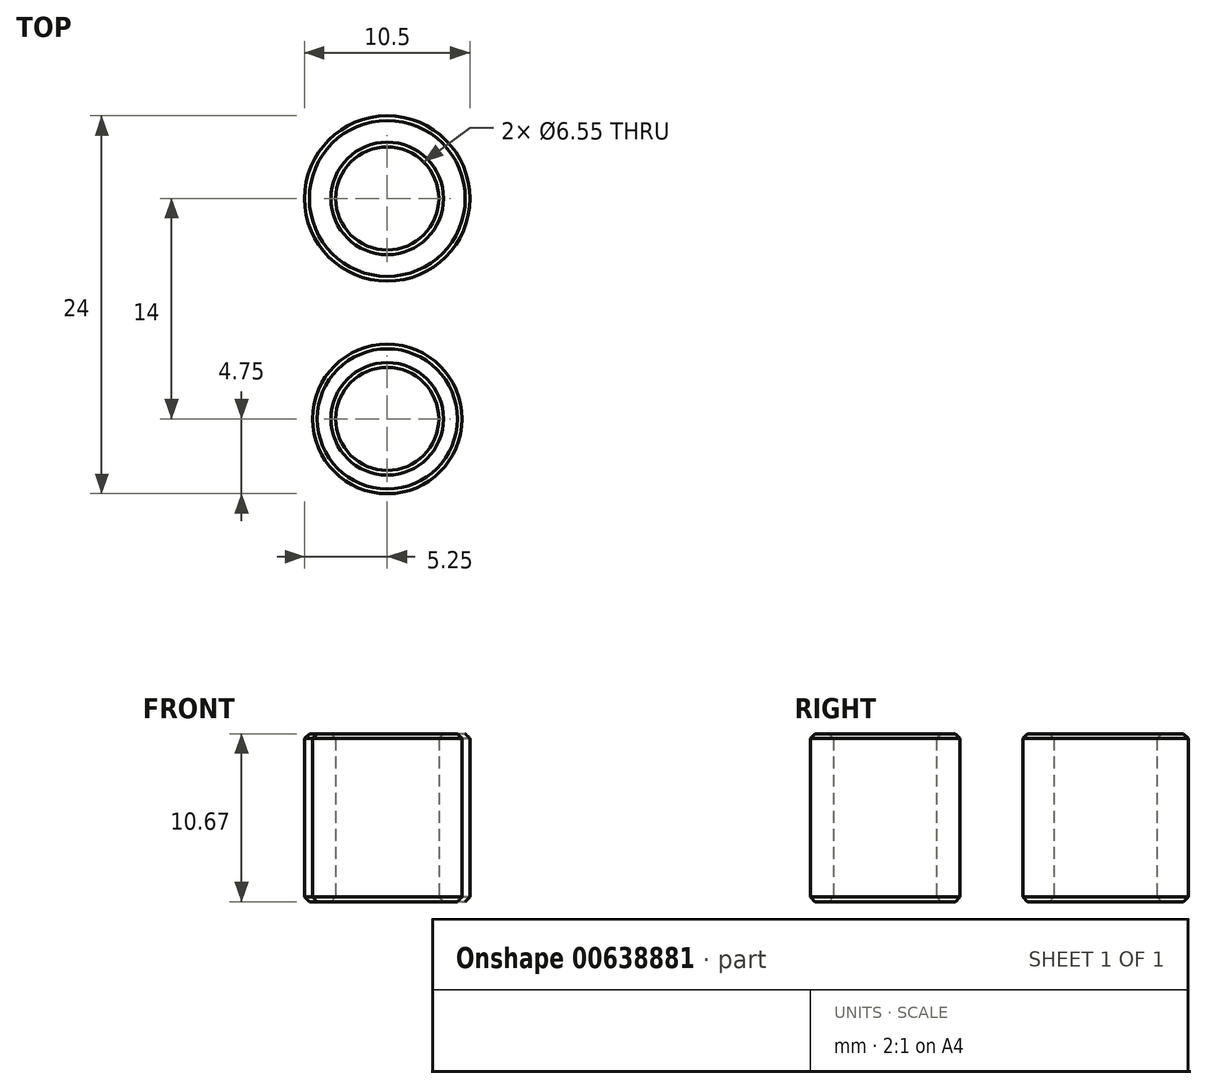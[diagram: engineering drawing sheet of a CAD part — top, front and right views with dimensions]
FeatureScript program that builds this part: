
annotation { "Feature Type Name" : "Feature", "Feature Type Description" : "" }
export const myFeature = defineFeature(function(context is Context, id is Id, definition is map)
    precondition{}
    {
        {
            var Q0;
            Q0=qCreatedBy(makeId("Top.planeOp"),FACE);
            var sketch = newSketch(context, id + "F0", { "sketchPlane" : qUnion([Q0])});
            skLineSegment(sketch, "E0", {"start": v(0, 0) * mm, "end": v(0, 15.25) * mm, "construction": true});
            skLineSegment(sketch, "E1", {"start": v(0, 15.25) * mm, "end": v(0, 31.75) * mm, "construction": true});
            skLineSegment(sketch, "E2", {"start": v(0, 0) * mm, "end": v(0, -14) * mm, "construction": true});
            skLineSegment(sketch, "E3", {"start": v(0, -14) * mm, "end": v(0, -27) * mm, "construction": true});
            skCircle(sketch, "E4", {"center": v(0, 31.75) * mm, "radius": 6.5 * mm});
            skCircle(sketch, "E5", {"center": v(0, 15.25) * mm, "radius": 6 * mm});
            skCircle(sketch, "E6", {"center": v(0, 0) * mm, "radius": 5.25 * mm});
            skCircle(sketch, "E7", {"center": v(0, -14) * mm, "radius": 4.75 * mm});
            skCircle(sketch, "E8", {"center": v(0, -27) * mm, "radius": 4.25 * mm});
            skCircle(sketch, "E9", {"center": v(0, 31.75) * mm, "radius": 3.28 * mm});
            skCircle(sketch, "E10", {"center": v(0, 15.25) * mm, "radius": 3.28 * mm});
            skCircle(sketch, "E11", {"center": v(0, 0) * mm, "radius": 3.28 * mm});
            skCircle(sketch, "E12", {"center": v(0, -14) * mm, "radius": 3.28 * mm});
            skCircle(sketch, "E13", {"center": v(0, -27) * mm, "radius": 3.28 * mm});
            skLineSegment(sketch, "E14", {"start": v(0, 31.75) * mm, "end": v(0, 49.25) * mm, "construction": true});
            skLineSegment(sketch, "E15", {"start": v(0, 49.25) * mm, "end": v(0, 67.75) * mm, "construction": true});
            skCircle(sketch, "E16", {"center": v(0, 49.25) * mm, "radius": 7 * mm});
            skCircle(sketch, "E17", {"center": v(0, 67.75) * mm, "radius": 7.5 * mm});
            skCircle(sketch, "E18", {"center": v(0, 49.25) * mm, "radius": 3.28 * mm});
            skCircle(sketch, "E19", {"center": v(0, 67.75) * mm, "radius": 3.28 * mm});
            skLineSegment(sketch, "E20", {"start": v(0, 67.75) * mm, "end": v(0, 87.25) * mm, "construction": true});
            skCircle(sketch, "E21", {"center": v(0, 87.25) * mm, "radius": 3.28 * mm});
            skCircle(sketch, "E22", {"center": v(0, 87.25) * mm, "radius": 8 * mm});
            skSolve(sketch);
        }
        {
            var Q0;
            Q0=makeQuery(id+"F0.imprint","IMPRINT",FACE,{"disambiguationData":[TD([[makeQuery(id+"F0.imprint","IMPRINT",EDGE,{"derivedFrom":sQuery(id+"F0.wireOp",EDGE,"E7")}),1.0]])]});
            var Q1;
            Q1=makeQuery(id+"F0.imprint","IMPRINT",FACE,{"disambiguationData":[TD([[makeQuery(id+"F0.imprint","IMPRINT",EDGE,{"derivedFrom":sQuery(id+"F0.wireOp",EDGE,"E6")}),1.0]])]});
            extrude(context, id + "F1", {"entities" : qUnion([Q0, Q1]), "depth" : 10.67 * mm, "offsetDistance" : 25 * mm});
        }
        {
            var Q0;
            Q0=makeQuery(id+"F1.opExtrude","CAP_EDGE",EDGE,{"disambiguationData":[OSD([sQuery(id+"F0.wireOp",EDGE,"E12")])],"isStart":false});
            var Q1;
            Q1=makeQuery(id+"F1.opExtrude","CAP_EDGE",EDGE,{"disambiguationData":[OSD([sQuery(id+"F0.wireOp",EDGE,"E11")])],"isStart":false});
            var Q2;
            Q2=makeQuery(id+"F1.opExtrude","CAP_EDGE",EDGE,{"disambiguationData":[OSD([sQuery(id+"F0.wireOp",EDGE,"E10")])],"isStart":false});
            var Q3;
            Q3=makeQuery(id+"F1.opExtrude","CAP_EDGE",EDGE,{"disambiguationData":[OSD([sQuery(id+"F0.wireOp",EDGE,"E9")])],"isStart":false});
            var Q4;
            Q4=makeQuery(id+"F1.opExtrude","CAP_EDGE",EDGE,{"disambiguationData":[OSD([sQuery(id+"F0.wireOp",EDGE,"E18")])],"isStart":false});
            var Q5;
            Q5=makeQuery(id+"F1.opExtrude","CAP_EDGE",EDGE,{"disambiguationData":[OSD([sQuery(id+"F0.wireOp",EDGE,"E19")])],"isStart":false});
            var Q6;
            Q6=makeQuery(id+"F1.opExtrude","CAP_EDGE",EDGE,{"disambiguationData":[OSD([sQuery(id+"F0.wireOp",EDGE,"E21")])],"isStart":false});
            var Q7;
            Q7=makeQuery(id+"F1.opExtrude","CAP_EDGE",EDGE,{"disambiguationData":[OSD([sQuery(id+"F0.wireOp",EDGE,"E21")])],"isStart":true});
            var Q8;
            Q8=makeQuery(id+"F1.opExtrude","CAP_EDGE",EDGE,{"disambiguationData":[OSD([sQuery(id+"F0.wireOp",EDGE,"E19")])],"isStart":true});
            var Q9;
            Q9=makeQuery(id+"F1.opExtrude","CAP_EDGE",EDGE,{"disambiguationData":[OSD([sQuery(id+"F0.wireOp",EDGE,"E18")])],"isStart":true});
            var Q10;
            Q10=makeQuery(id+"F1.opExtrude","CAP_EDGE",EDGE,{"disambiguationData":[OSD([sQuery(id+"F0.wireOp",EDGE,"E9")])],"isStart":true});
            var Q11;
            Q11=makeQuery(id+"F1.opExtrude","CAP_EDGE",EDGE,{"disambiguationData":[OSD([sQuery(id+"F0.wireOp",EDGE,"E10")])],"isStart":true});
            var Q12;
            Q12=makeQuery(id+"F1.opExtrude","CAP_EDGE",EDGE,{"disambiguationData":[OSD([sQuery(id+"F0.wireOp",EDGE,"E11")])],"isStart":true});
            var Q13;
            Q13=makeQuery(id+"F1.opExtrude","CAP_EDGE",EDGE,{"disambiguationData":[OSD([sQuery(id+"F0.wireOp",EDGE,"E12")])],"isStart":true});
            var Q14;
            Q14=makeQuery(id+"F1.opExtrude","CAP_EDGE",EDGE,{"disambiguationData":[OSD([sQuery(id+"F0.wireOp",EDGE,"E5")])],"isStart":true});
            var Q15;
            Q15=makeQuery(id+"F1.opExtrude","CAP_EDGE",EDGE,{"disambiguationData":[OSD([sQuery(id+"F0.wireOp",EDGE,"E4")])],"isStart":true});
            var Q16;
            Q16=makeQuery(id+"F1.opExtrude","CAP_EDGE",EDGE,{"disambiguationData":[OSD([sQuery(id+"F0.wireOp",EDGE,"E16")])],"isStart":true});
            var Q17;
            Q17=makeQuery(id+"F1.opExtrude","CAP_EDGE",EDGE,{"disambiguationData":[OSD([sQuery(id+"F0.wireOp",EDGE,"E17")])],"isStart":true});
            var Q18;
            Q18=makeQuery(id+"F1.opExtrude","CAP_EDGE",EDGE,{"disambiguationData":[OSD([sQuery(id+"F0.wireOp",EDGE,"E22")])],"isStart":true});
            var Q19;
            Q19=makeQuery(id+"F1.opExtrude","CAP_EDGE",EDGE,{"disambiguationData":[OSD([sQuery(id+"F0.wireOp",EDGE,"E13")])],"isStart":true});
            var Q20;
            Q20=makeQuery(id+"F1.opExtrude","CAP_EDGE",EDGE,{"disambiguationData":[OSD([sQuery(id+"F0.wireOp",EDGE,"E7")])],"isStart":true});
            var Q21;
            Q21=makeQuery(id+"F1.opExtrude","CAP_EDGE",EDGE,{"disambiguationData":[OSD([sQuery(id+"F0.wireOp",EDGE,"E6")])],"isStart":true});
            var Q22;
            Q22=makeQuery(id+"F1.opExtrude","CAP_EDGE",EDGE,{"disambiguationData":[OSD([sQuery(id+"F0.wireOp",EDGE,"E8")])],"isStart":true});
            var Q23;
            Q23=makeQuery(id+"F1.opExtrude","CAP_EDGE",EDGE,{"disambiguationData":[OSD([sQuery(id+"F0.wireOp",EDGE,"E8")])],"isStart":false});
            var Q24;
            Q24=makeQuery(id+"F1.opExtrude","CAP_EDGE",EDGE,{"disambiguationData":[OSD([sQuery(id+"F0.wireOp",EDGE,"E13")])],"isStart":false});
            var Q25;
            Q25=makeQuery(id+"F1.opExtrude","CAP_EDGE",EDGE,{"disambiguationData":[OSD([sQuery(id+"F0.wireOp",EDGE,"E7")])],"isStart":false});
            var Q26;
            Q26=makeQuery(id+"F1.opExtrude","CAP_EDGE",EDGE,{"disambiguationData":[OSD([sQuery(id+"F0.wireOp",EDGE,"E6")])],"isStart":false});
            chamfer(context, id + "F2", {"entities" : qUnion([Q0, Q1, Q2, Q3, Q4, Q5, Q6, Q7, Q8, Q9, Q10, Q11, Q12, Q13, Q14, Q15, Q16, Q17, Q18, Q19, Q20, Q21, Q22, Q23, Q24, Q25, Q26]), "width" : 0.3 * mm, "tangentPropagation" : true});
        }
    });
